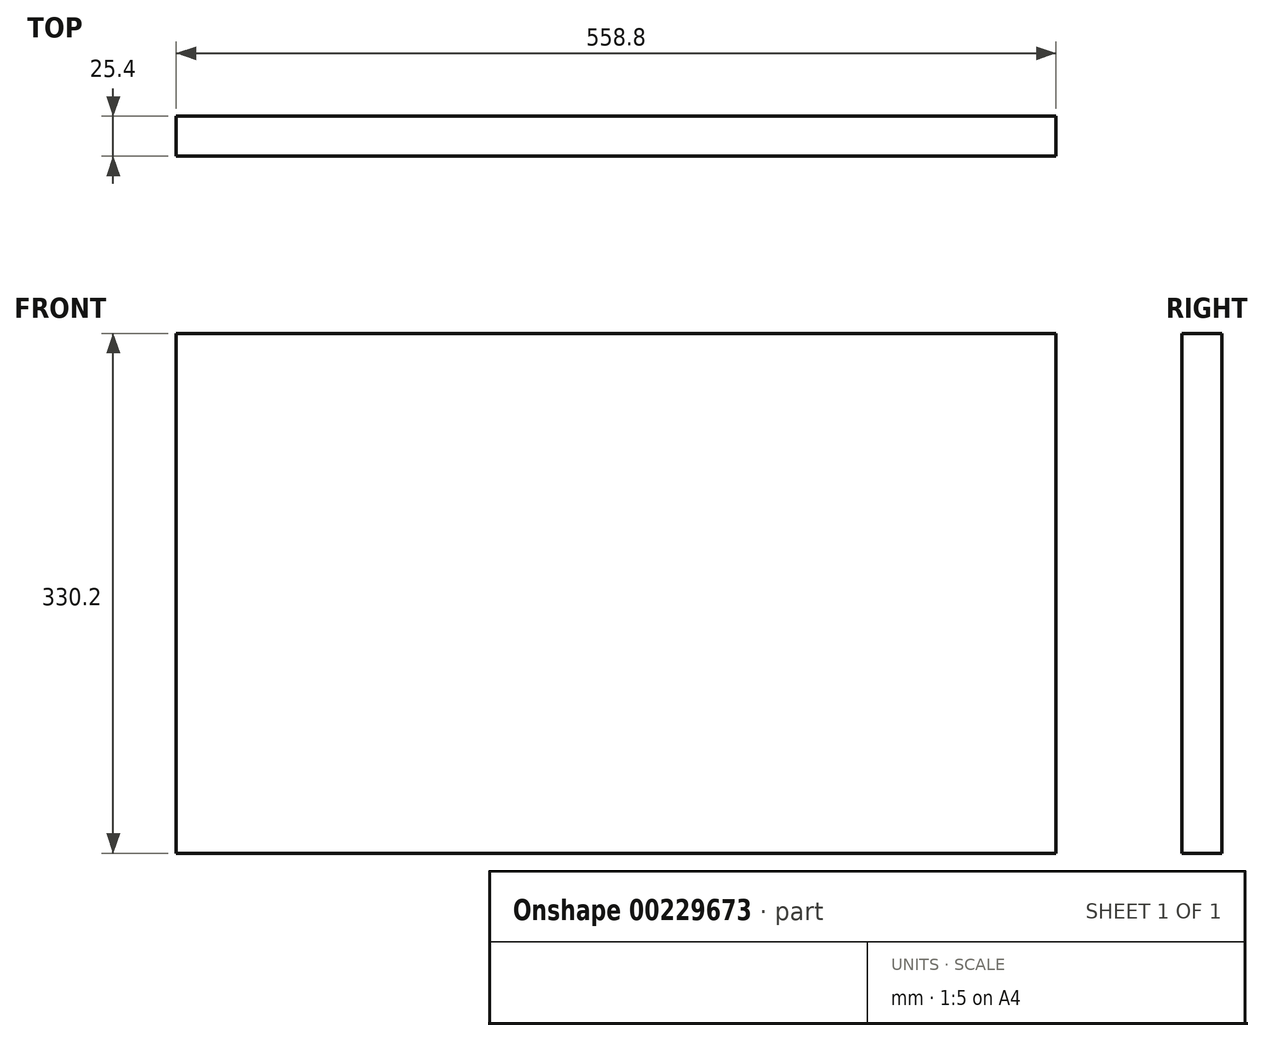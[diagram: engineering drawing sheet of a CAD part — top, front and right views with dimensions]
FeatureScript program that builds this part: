
annotation { "Feature Type Name" : "Feature", "Feature Type Description" : "" }
export const myFeature = defineFeature(function(context is Context, id is Id, definition is map)
    precondition{}
    {
        {
            var Q0;
            Q0=qCreatedBy(makeId("Front.planeOp"),FACE);
            var sketch = newSketch(context, id + "F0", { "sketchPlane" : qUnion([Q0])});
            skLineSegment(sketch, "E0", {"start": v(0, 0) * mm, "end": v(279.4, 0) * mm});
            skLineSegment(sketch, "E1", {"start": v(0, 0) * mm, "end": v(-279.4, 0) * mm});
            skLineSegment(sketch, "E2", {"start": v(-279.4, 0) * mm, "end": v(-279.4, -330.2) * mm});
            skLineSegment(sketch, "E3", {"start": v(-279.4, -330.2) * mm, "end": v(279.4, -330.2) * mm});
            skLineSegment(sketch, "E4", {"start": v(279.4, -330.2) * mm, "end": v(279.4, 0) * mm});
            skSolve(sketch);
        }
        {
            var Q0;
            Q0 = qSketchRegion(id + "F0", true);
            extrude(context, id + "F1", {"entities" : qUnion([Q0]), "depth" : 25.4 * mm});
        }
    });
